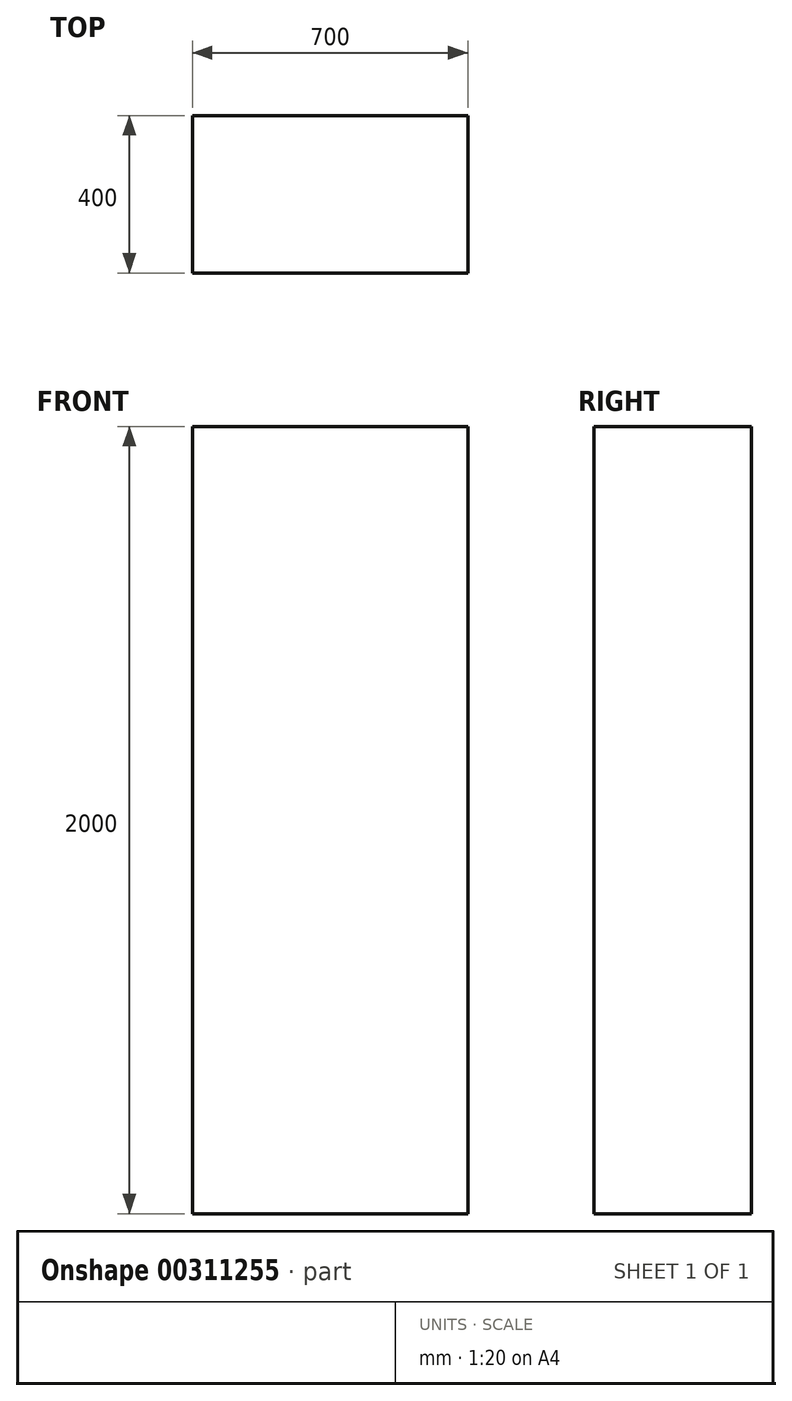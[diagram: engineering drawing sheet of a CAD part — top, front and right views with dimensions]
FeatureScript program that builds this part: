
annotation { "Feature Type Name" : "Feature", "Feature Type Description" : "" }
export const myFeature = defineFeature(function(context is Context, id is Id, definition is map)
    precondition{}
    {
        {
            var Q0;
            Q0=qCreatedBy(makeId("Front.planeOp"),FACE);
            var sketch = newSketch(context, id + "F0", { "sketchPlane" : qUnion([Q0])});
            skLineSegment(sketch, "E0.bottom", {"start": v(0, 0) * mm, "end": v(700, 0) * mm});
            skLineSegment(sketch, "E0.top", {"start": v(0, 2000) * mm, "end": v(700, 2000) * mm});
            skLineSegment(sketch, "E0.left", {"start": v(0, 0) * mm, "end": v(0, 2000) * mm});
            skLineSegment(sketch, "E0.right", {"start": v(700, 0) * mm, "end": v(700, 2000) * mm});
            skSolve(sketch);
        }
        {
            var Q0;
            Q0=makeQuery(id+"F0.imprint","IMPRINT",FACE,{"disambiguationData":[TD([[makeQuery(id+"F0.imprint","IMPRINT",EDGE,{"derivedFrom":sQuery(id+"F0.wireOp",EDGE,"E0.bottom")}),1.0]])]});
            extrude(context, id + "F1", {"entities" : qUnion([Q0]), "oppositeDirection" : true, "depth" : 400 * mm});
        }
    });
